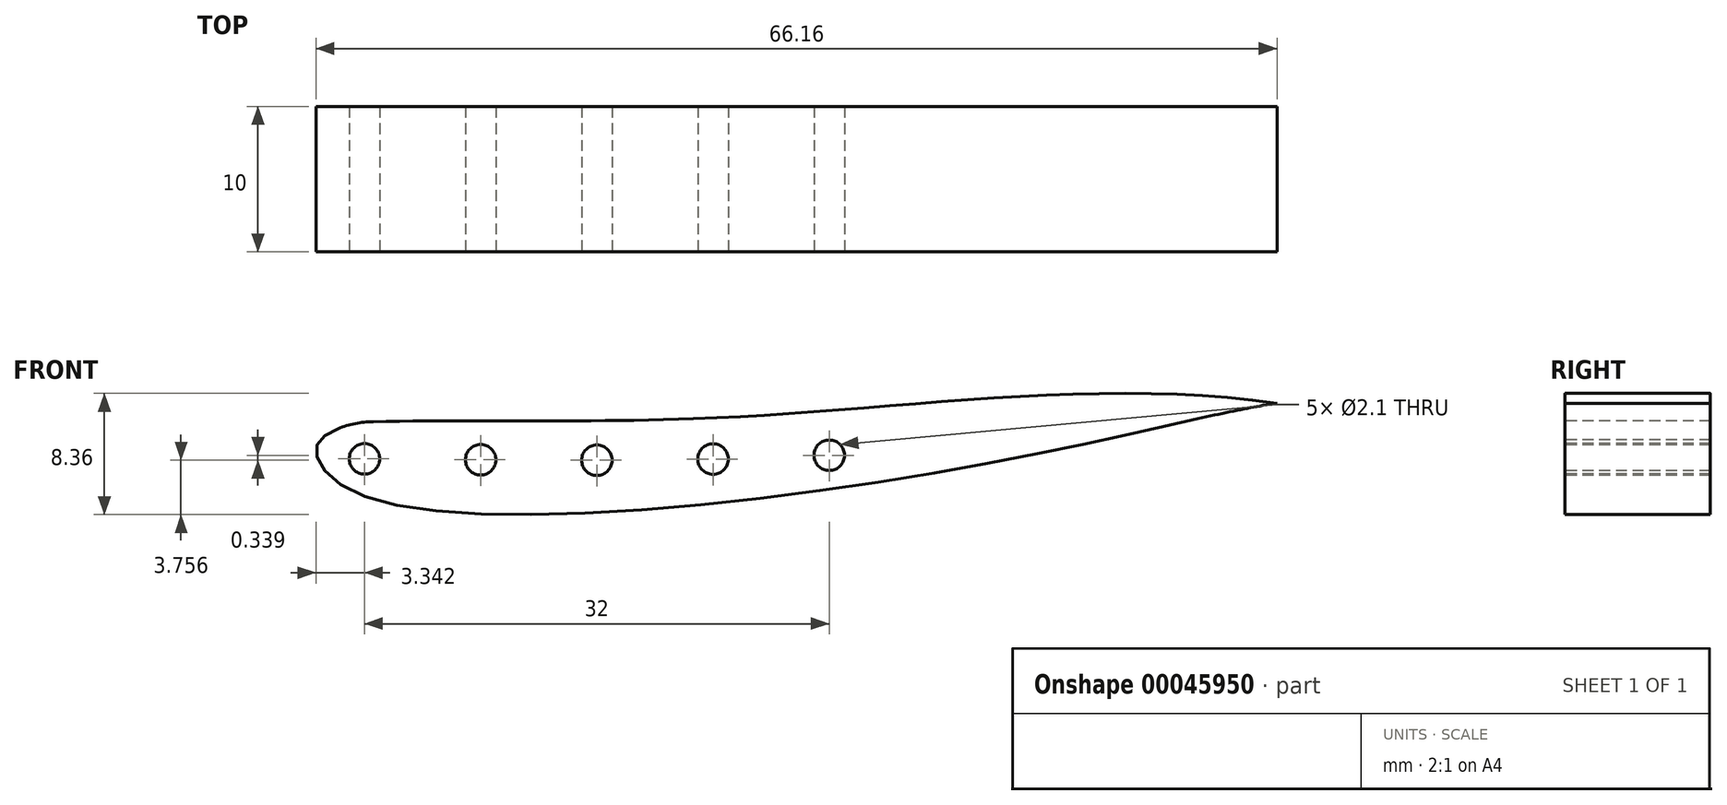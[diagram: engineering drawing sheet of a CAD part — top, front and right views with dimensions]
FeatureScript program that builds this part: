
annotation { "Feature Type Name" : "Feature", "Feature Type Description" : "" }
export const myFeature = defineFeature(function(context is Context, id is Id, definition is map)
    precondition{}
    {
        {
            var Q0;
            Q0=qCreatedBy(makeId("Front.planeOp"),FACE);
            var sketch = newSketch(context, id + "F0", { "sketchPlane" : qUnion([Q0])});
            skFitSpline(sketch, "E0", {"points": [v(-21.5, 15.59) * mm, v(6.04, 16.02) * mm, v(44.7, 16.34) * mm], "startDerivative": vector(56.58, 1.46) * mm, "endDerivative": vector(65.86, -14.19) * mm});
            skFitSpline(sketch, "E1", {"points": [v(-21.5, 15.59) * mm, v(-24.32, 14.06) * mm, v(-21.5, 10.64) * mm, v(19.63, 12.33) * mm, v(41.74, 16.88) * mm], "startDerivative": vector(-28.74, -8.85) * mm, "endDerivative": vector(37.64, 5.09) * mm});
            skLineSegment(sketch, "E2", {"start": v(-12.88, 15.81) * mm, "end": v(36.3, 15.81) * mm});
            skLineSegment(sketch, "E3.trimOffspring", {"start": v(41.74, 16.88) * mm, "end": v(41.74, 16.88) * mm});
            skSolve(sketch);
        }
        {
            var Q0;
            Q0=makeQuery(id+"F0.imprint","IMPRINT",FACE,{"disambiguationData":[TD([[makeQuery(id+"F0.imprint","IMPRINT",EDGE,{"derivedFrom":sQuery(id+"F0.wireOp",EDGE,"E0")}),-1.0]])]});
            extrude(context, id + "F1", {"entities" : qUnion([Q0]), "depth" : 10 * mm});
        }
        {
            var Q0;
            {var subQ0=sQuery(id+"F0.wireOp",EDGE,"E1");var subQ1=sQuery(id+"F0.wireOp",EDGE,"E0");Q0=makeQuery(id+"F1.opExtrude","SWEPT_EDGE",EDGE,{"disambiguationData":[OSD([subQ1,subQ0]),TDD([makeQuery(id+"F0.imprint","INTERSECT",VERTEX,{"disambiguationData":[OD(0.0)],"derivedFrom":[subQ1,subQ0]})])]});}
            fillet(context, id + "F2", {"entities" : qUnion([Q0]), "radius" : 6.9 * mm, "tangentPropagation" : true, "allowEdgeOverflow" : false});
        }
        {
            var Q0;
            Q0=makeQuery(id+"F1.opExtrude","CAP_FACE",FACE,{"disambiguationData":[OSD([sQuery(id+"F0.wireOp",EDGE,"E0"),sQuery(id+"F0.wireOp",EDGE,"E1")])],"isStart":false});
            var sketch = newSketch(context, id + "F3", { "sketchPlane" : qUnion([Q0])});
            skCircle(sketch, "E4", {"center": v(-21.08, 13.05) * mm, "radius": 1.05 * mm});
            skCircle(sketch, "E5", {"center": v(-13.08, 12.98) * mm, "radius": 1.05 * mm});
            skCircle(sketch, "E6", {"center": v(2.92, 13.03) * mm, "radius": 1.05 * mm});
            skCircle(sketch, "E7", {"center": v(10.92, 13.3) * mm, "radius": 1.05 * mm});
            skPoint(sketch, "E8.center.orphan", {"position": v(0, 20.97) * mm});
            skCircle(sketch, "E9", {"center": v(-5.08, 12.96) * mm, "radius": 1.05 * mm});
            skSolve(sketch);
        }
        {
            var Q0;
            Q0=makeQuery(id+"F3.imprint","IMPRINT",FACE,{"disambiguationData":[TD([[makeQuery(id+"F3.imprint","IMPRINT",EDGE,{"derivedFrom":sQuery(id+"F3.wireOp",EDGE,"E4")}),1.0]])]});
            var Q1;
            Q1=makeQuery(id+"F3.imprint","IMPRINT",FACE,{"disambiguationData":[TD([[makeQuery(id+"F3.imprint","IMPRINT",EDGE,{"derivedFrom":sQuery(id+"F3.wireOp",EDGE,"E6")}),1.0]])]});
            var Q2;
            Q2=makeQuery(id+"F3.imprint","IMPRINT",FACE,{"disambiguationData":[TD([[makeQuery(id+"F3.imprint","IMPRINT",EDGE,{"derivedFrom":sQuery(id+"F3.wireOp",EDGE,"E5")}),1.0]])]});
            var Q3;
            Q3=makeQuery(id+"F3.imprint","IMPRINT",FACE,{"disambiguationData":[TD([[makeQuery(id+"F3.imprint","IMPRINT",EDGE,{"derivedFrom":sQuery(id+"F3.wireOp",EDGE,"E9")}),1.0]])]});
            var Q4;
            Q4=makeQuery(id+"F3.imprint","IMPRINT",FACE,{"disambiguationData":[TD([[makeQuery(id+"F3.imprint","IMPRINT",EDGE,{"derivedFrom":sQuery(id+"F3.wireOp",EDGE,"E7")}),1.0]])]});
            extrude(context, id + "F4", {"entities" : qUnion([Q0, Q1, Q2, Q3, Q4]), "operationType" : NewBodyOperationType.REMOVE, "oppositeDirection" : true, "depth" : 25 * mm});
        }
    });
